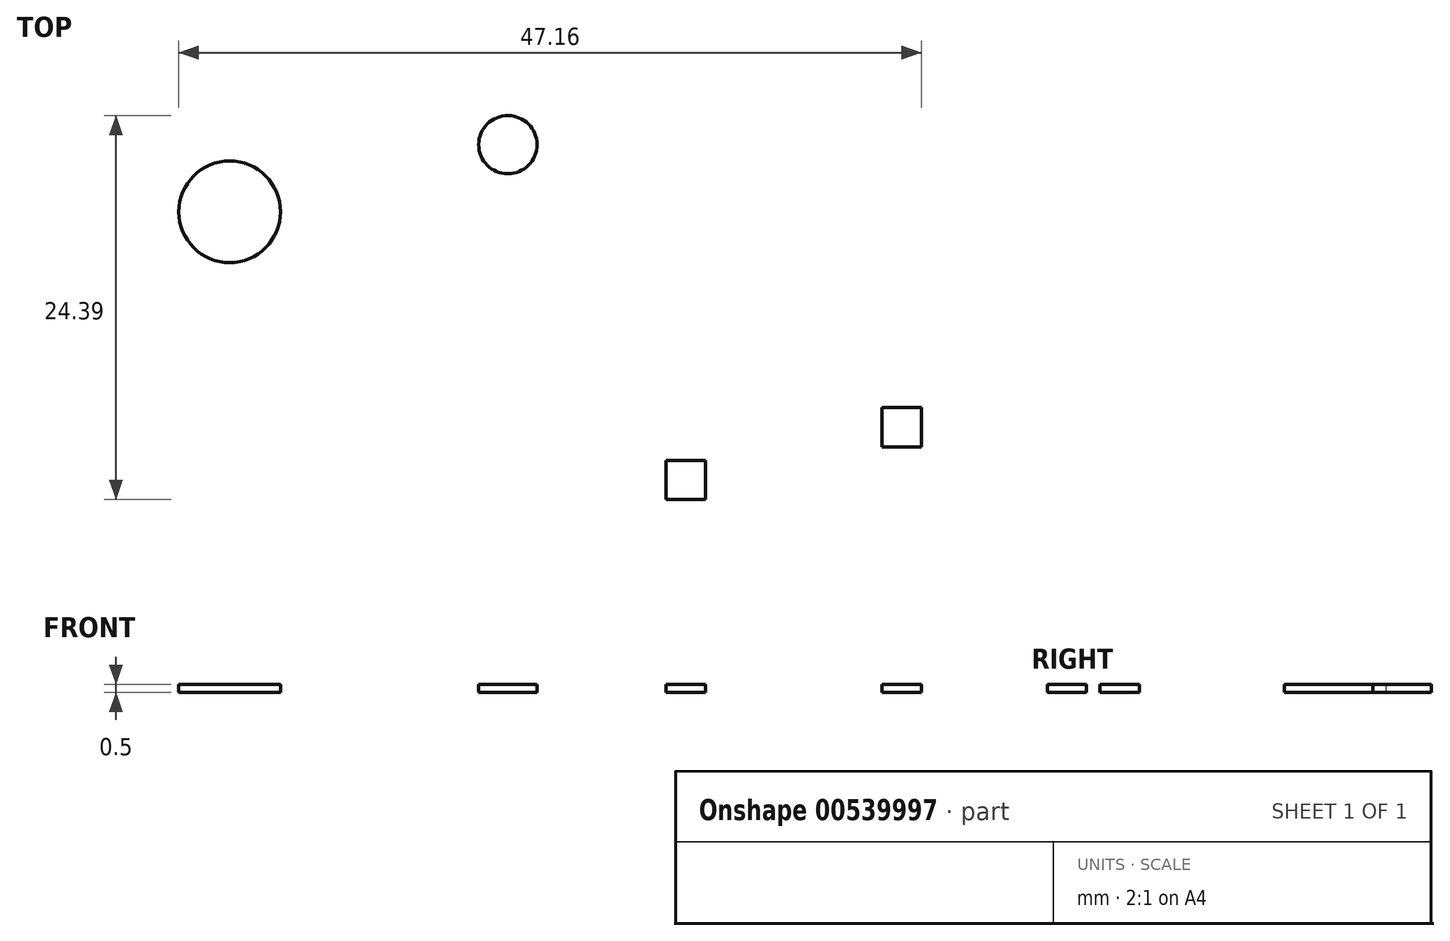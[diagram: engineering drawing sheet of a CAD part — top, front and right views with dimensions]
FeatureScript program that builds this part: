
annotation { "Feature Type Name" : "Feature", "Feature Type Description" : "" }
export const myFeature = defineFeature(function(context is Context, id is Id, definition is map)
    precondition{}
    {
        {
            var Q0;
            Q0=qCreatedBy(makeId("Top.planeOp"),FACE);
            var sketch = newSketch(context, id + "F0", { "sketchPlane" : qUnion([Q0])});
            skCircle(sketch, "E0", {"center": v(-51.48, 41.58) * mm, "radius": 3.23 * mm});
            skCircle(sketch, "E1", {"center": v(-33.82, 45.85) * mm, "radius": 1.85 * mm});
            skLineSegment(sketch, "E2.bottom", {"start": v(-21.26, 23.3) * mm, "end": v(-23.76, 23.3) * mm});
            skLineSegment(sketch, "E2.top", {"start": v(-21.26, 25.8) * mm, "end": v(-23.76, 25.8) * mm});
            skLineSegment(sketch, "E2.left", {"start": v(-21.26, 23.3) * mm, "end": v(-21.26, 25.8) * mm});
            skLineSegment(sketch, "E2.right", {"start": v(-23.76, 23.3) * mm, "end": v(-23.76, 25.8) * mm});
            skPoint(sketch, "E2.middle", {"position": v(-22.51, 24.56) * mm});
            skLineSegment(sketch, "E3.bottom", {"start": v(-7.55, 29.16) * mm, "end": v(-10.05, 29.16) * mm});
            skLineSegment(sketch, "E3.top", {"start": v(-7.55, 26.66) * mm, "end": v(-10.05, 26.66) * mm});
            skLineSegment(sketch, "E3.left", {"start": v(-7.55, 29.16) * mm, "end": v(-7.55, 26.66) * mm});
            skLineSegment(sketch, "E3.right", {"start": v(-10.05, 29.16) * mm, "end": v(-10.05, 26.66) * mm});
            skPoint(sketch, "E3.middle", {"position": v(-8.8, 27.9) * mm});
            skSolve(sketch);
        }
        {
            var Q0;
            Q0 = qSketchRegion(id + "F0", true);
            extrude(context, id + "F1", {"entities" : qUnion([Q0]), "depth" : .5 * mm, "offsetDistance" : 25 * mm});
        }
    });
